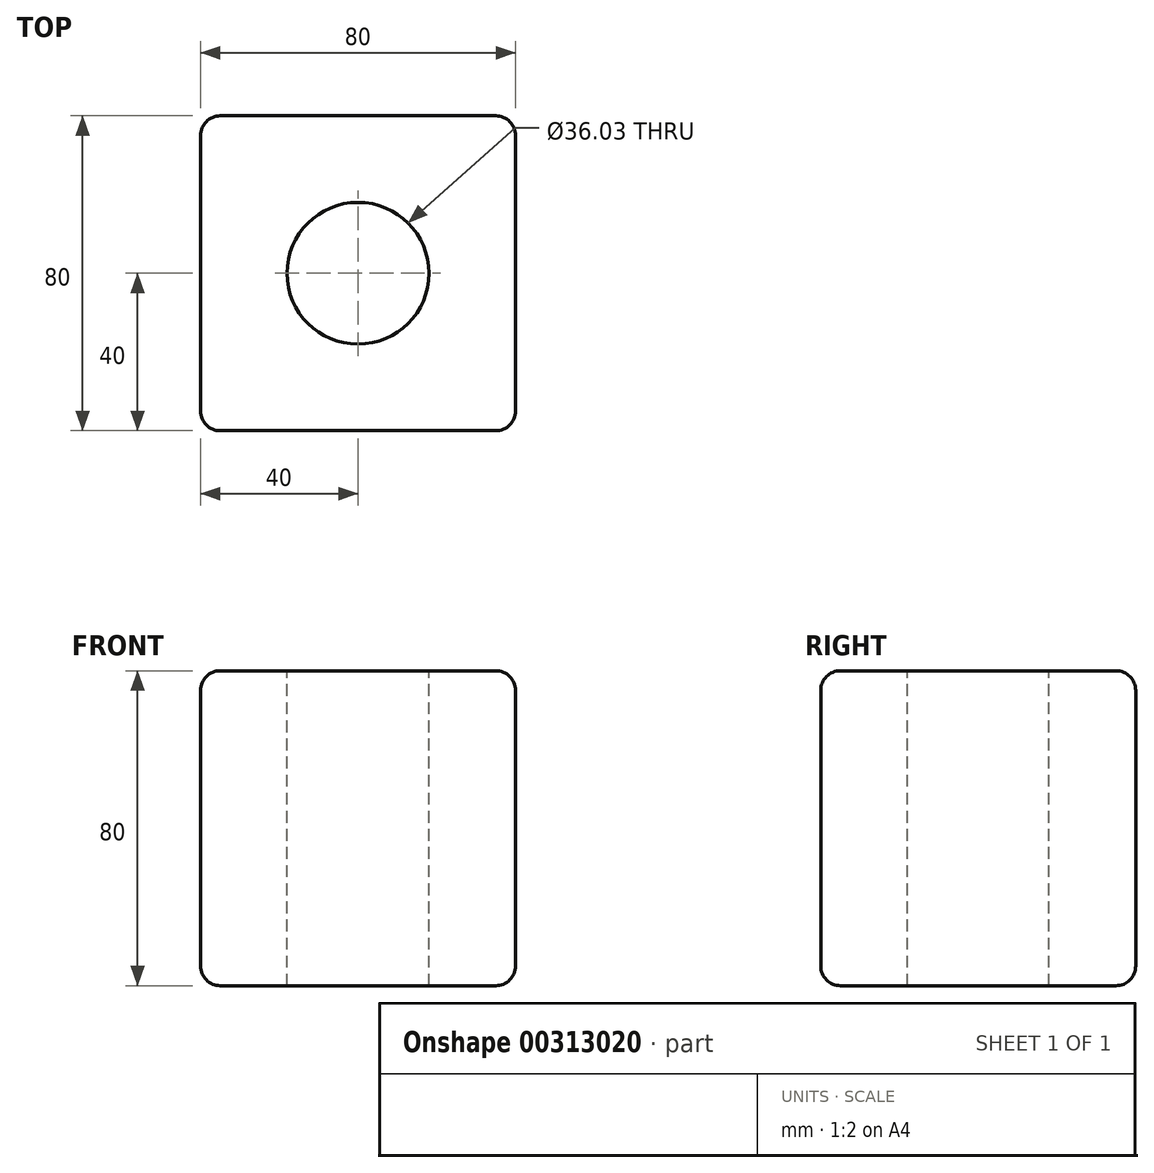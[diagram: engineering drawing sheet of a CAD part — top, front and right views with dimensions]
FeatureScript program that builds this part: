
annotation { "Feature Type Name" : "Feature", "Feature Type Description" : "" }
export const myFeature = defineFeature(function(context is Context, id is Id, definition is map)
    precondition{}
    {
        {
            var Q0;
            Q0=qCreatedBy(makeId("Top.planeOp"),FACE);
            var sketch = newSketch(context, id + "F0", { "sketchPlane" : qUnion([Q0])});
            skLineSegment(sketch, "E0.bottom", {"start": v(-40, 40) * mm, "end": v(40, 40) * mm});
            skLineSegment(sketch, "E0.top", {"start": v(-40, -40) * mm, "end": v(40, -40) * mm});
            skLineSegment(sketch, "E0.left", {"start": v(-40, 40) * mm, "end": v(-40, -40) * mm});
            skLineSegment(sketch, "E0.right", {"start": v(40, 40) * mm, "end": v(40, -40) * mm});
            skPoint(sketch, "E0.middle", {"position": v(0, 0) * mm});
            skSolve(sketch);
        }
        {
            var Q0;
            Q0=makeQuery(id+"F0.imprint","IMPRINT",FACE,{"disambiguationData":[TD([[makeQuery(id+"F0.imprint","IMPRINT",EDGE,{"derivedFrom":sQuery(id+"F0.wireOp",EDGE,"E0.bottom")}),-1.0]])]});
            extrude(context, id + "F1", {"entities" : qUnion([Q0]), "endBound" : BoundingType.SYMMETRIC, "depth" : 80 * mm});
        }
        {
            var Q0;
            Q0=makeQuery(id+"F1.opExtrude","CAP_EDGE",EDGE,{"disambiguationData":[OSD([sQuery(id+"F0.wireOp",EDGE,"E0.left")])],"isStart":false});
            var Q1;
            Q1=makeQuery(id+"F1.opExtrude","CAP_EDGE",EDGE,{"disambiguationData":[OSD([sQuery(id+"F0.wireOp",EDGE,"E0.top")])],"isStart":false});
            var Q2;
            Q2=makeQuery(id+"F1.opExtrude","CAP_EDGE",EDGE,{"disambiguationData":[OSD([sQuery(id+"F0.wireOp",EDGE,"E0.right")])],"isStart":false});
            var Q3;
            Q3=makeQuery(id+"F1.opExtrude","CAP_EDGE",EDGE,{"disambiguationData":[OSD([sQuery(id+"F0.wireOp",EDGE,"E0.bottom")])],"isStart":false});
            var Q4;
            Q4=makeQuery(id+"F1.opExtrude","SWEPT_EDGE",EDGE,{"disambiguationData":[OSD([sQuery(id+"F0.wireOp",EDGE,"E0.top"),sQuery(id+"F0.wireOp",EDGE,"E0.right")])]});
            var Q5;
            Q5=makeQuery(id+"F1.opExtrude","CAP_EDGE",EDGE,{"disambiguationData":[OSD([sQuery(id+"F0.wireOp",EDGE,"E0.right")])],"isStart":true});
            var Q6;
            Q6=makeQuery(id+"F1.opExtrude","CAP_EDGE",EDGE,{"disambiguationData":[OSD([sQuery(id+"F0.wireOp",EDGE,"E0.top")])],"isStart":true});
            var Q7;
            Q7=makeQuery(id+"F1.opExtrude","SWEPT_EDGE",EDGE,{"disambiguationData":[OSD([sQuery(id+"F0.wireOp",EDGE,"E0.top"),sQuery(id+"F0.wireOp",EDGE,"E0.left")])]});
            var Q8;
            Q8=makeQuery(id+"F1.opExtrude","CAP_EDGE",EDGE,{"disambiguationData":[OSD([sQuery(id+"F0.wireOp",EDGE,"E0.left")])],"isStart":true});
            var Q9;
            Q9=makeQuery(id+"F1.opExtrude","CAP_EDGE",EDGE,{"disambiguationData":[OSD([sQuery(id+"F0.wireOp",EDGE,"E0.bottom")])],"isStart":true});
            var Q10;
            Q10=makeQuery(id+"F1.opExtrude","SWEPT_EDGE",EDGE,{"disambiguationData":[OSD([sQuery(id+"F0.wireOp",EDGE,"E0.bottom"),sQuery(id+"F0.wireOp",EDGE,"E0.left")])]});
            var Q11;
            Q11=makeQuery(id+"F1.opExtrude","SWEPT_EDGE",EDGE,{"disambiguationData":[OSD([sQuery(id+"F0.wireOp",EDGE,"E0.bottom"),sQuery(id+"F0.wireOp",EDGE,"E0.right")])]});
            fillet(context, id + "F2", {"entities" : qUnion([Q0, Q1, Q2, Q3, Q4, Q5, Q6, Q7, Q8, Q9, Q10, Q11]), "radius" : 5 * mm, "tangentPropagation" : true, "allowEdgeOverflow" : false});
        }
        {
            var Q0;
            Q0=makeQuery(id+"F1.opExtrude","CAP_FACE",FACE,{"disambiguationData":[OSD([sQuery(id+"F0.wireOp",EDGE,"E0.bottom"),sQuery(id+"F0.wireOp",EDGE,"E0.top"),sQuery(id+"F0.wireOp",EDGE,"E0.left"),sQuery(id+"F0.wireOp",EDGE,"E0.right")])],"isStart":false});
            var sketch = newSketch(context, id + "F3", { "sketchPlane" : qUnion([Q0])});
            skCircle(sketch, "E1", {"center": v(0, 0) * mm, "radius": 18.02 * mm});
            skSolve(sketch);
        }
        {
            var Q0;
            Q0=makeQuery(id+"F3.imprint","IMPRINT",FACE,{"disambiguationData":[TD([[makeQuery(id+"F3.imprint","IMPRINT",EDGE,{"derivedFrom":sQuery(id+"F3.wireOp",EDGE,"E1")}),1.0]])]});
            extrude(context, id + "F4", {"entities" : qUnion([Q0]), "operationType" : NewBodyOperationType.REMOVE, "endBound" : BoundingType.THROUGH_ALL, "oppositeDirection" : true, "depth" : 25 * mm});
        }
    });
